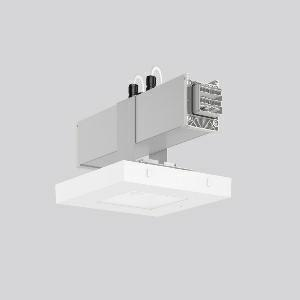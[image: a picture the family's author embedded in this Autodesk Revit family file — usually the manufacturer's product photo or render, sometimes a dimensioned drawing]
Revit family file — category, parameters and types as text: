
# Revit family: linedo_module_rf_9503rf_760_400_000_2908
name_source: partatom
category: Lighting Fixtures
units: mm (PartAtom-declared; Revit-internal decimal feet)

## family parameters
Cut with Voids When Loaded = No
Host = Face
Light Source = No
Part Type = Normal
Room Calculation Point = No
Round Connector Dimension = Use Diameter
Shared = No

## types (1)
- LINEDO Module RF (1 x LED Modul 765, 420 lm, 6500)
    Apparent Load = 6 VA
    CIE Flux Codes = 48 88 100 100 100
    Color Rendering = 70
    Color Temperature = 6500
    Default Elevation = 1800 mm
    Description = LINEDO, 5,7 W, 420 lm, 765, silver, on/off
Continuous line luminaire, L 330 B 198 H 170, CBS, emergency-420 lm, Stromkreis
    Height = 170 mm  [stored 0.557743 ft]
    Lamp = 1 x LED Modul 765
    Lamp Light Flux = 420 lm
    Lamp count = 1
    Length = 330 mm
    Lifetime = 50000 h
    Luminous efficacy = 74 lm/W
    Manufacturer = RZB
    ModVariant = No
    Model = 9503RF.760.400.000
    Mounting Place = Ceiling
    Mounting Type = Surface mounted, Pendant
    Number of Poles = 1
    OnlyDefault = Yes
    Power Factor = 1
    Product Name = LINEDO Module RF
    Product group = Continuous line luminaire system Linedo IP 54
    ProductGroupID = 314
    Protection Class = Protection class I
    Protection Degree = IP 54
    RLX_Detail_Level = 1
    RLX_Emergency_Light_Flux = 420 lm
    RLX_Emergency_Type = 3
    RLX_Emergency_Type_DB = Yes
    RlxData = <blob elided: 21633 chars, md5=caa71c53>
    Socket = socket
    Standby Power = 0 W
    System Light Flux = 420 lm
    System Power = 6 W
    Type Comments = Product without accessories
    Type Image = 9503rw.760.434.000.jpg
    URL = http://relux.com
    VarID = ---
    Voltage = 230 V
    Voltage Range = 220-240 V
    Weight = 0.00 kg
    Width = 198 mm

note: [stored X ft] marks values corroborated as IEEE doubles in the binary element streams (Revit-internal decimal feet)

## geometry (parser evidence)
native form markers: Blend x4, Sweep x16
no freeform markers — native parametric forms only
